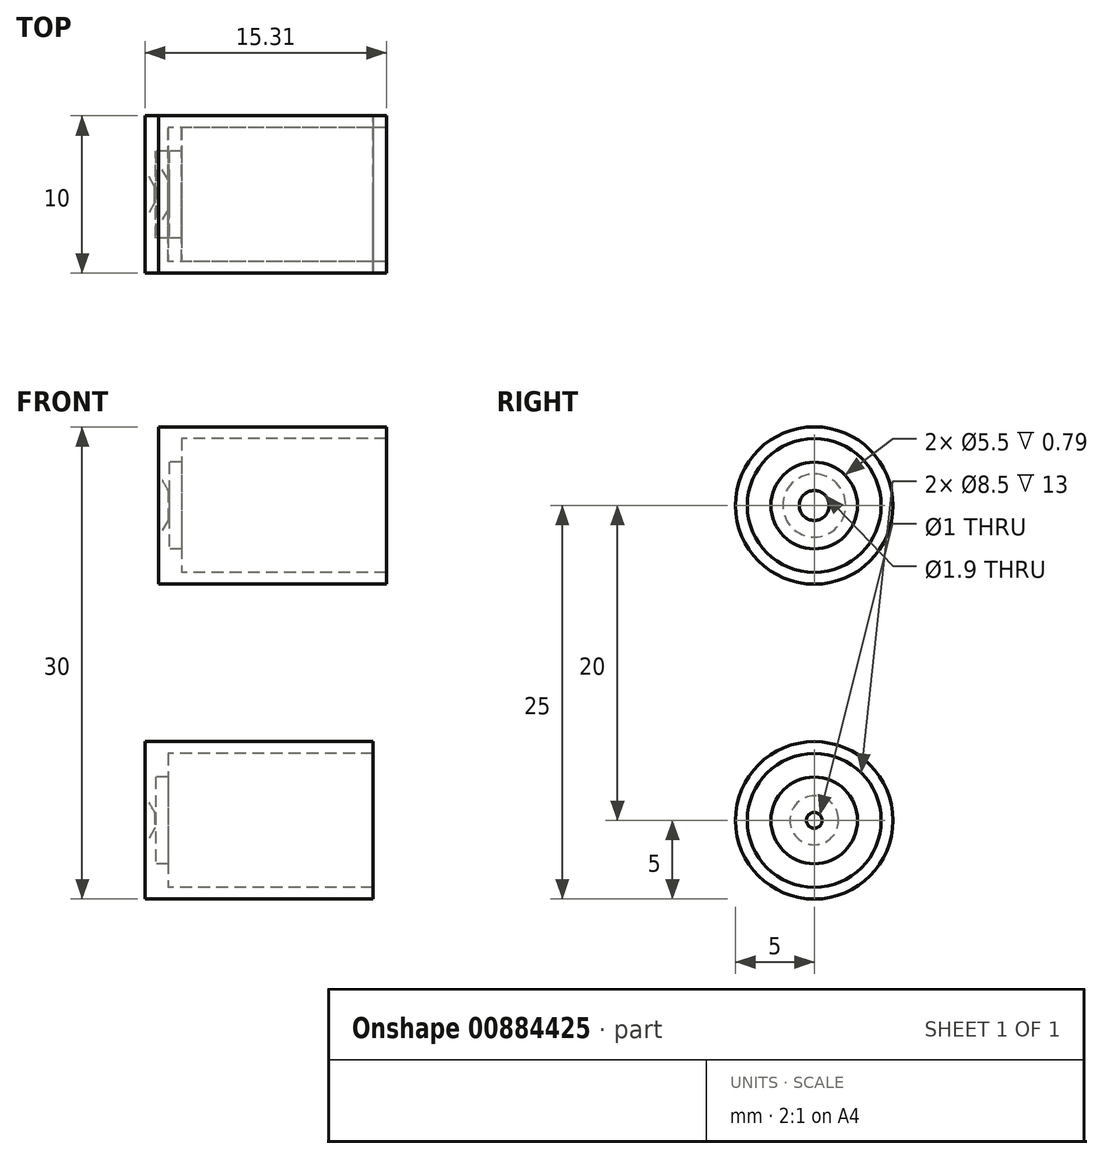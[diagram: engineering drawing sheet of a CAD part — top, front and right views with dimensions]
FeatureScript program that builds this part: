
annotation { "Feature Type Name" : "Feature", "Feature Type Description" : "" }
export const myFeature = defineFeature(function(context is Context, id is Id, definition is map)
    precondition{}
    {
        {
            var Q0;
            Q0=qCreatedBy(makeId("Front.planeOp"),FACE);
            var sketch = newSketch(context, id + "F0", { "sketchPlane" : qUnion([Q0])});
            skLineSegment(sketch, "E0", {"start": v(0, 0.95) * mm, "end": v(-0.6, 2) * mm});
            skLineSegment(sketch, "E1", {"start": v(-0.6, 2) * mm, "end": v(-0.6, 5) * mm});
            skLineSegment(sketch, "E2", {"start": v(-0.6, 5) * mm, "end": v(13.85, 5) * mm});
            skLineSegment(sketch, "E3", {"start": v(13.85, 5) * mm, "end": v(13.85, 4.25) * mm});
            skLineSegment(sketch, "E4", {"start": v(13.85, 4.25) * mm, "end": v(0.85, 4.25) * mm});
            skLineSegment(sketch, "E5", {"start": v(0.85, 4.25) * mm, "end": v(0.85, 2.75) * mm});
            skLineSegment(sketch, "E6", {"start": v(0.85, 2.75) * mm, "end": v(0.06, 2.75) * mm});
            skLineSegment(sketch, "E7", {"start": v(0.06, 2.75) * mm, "end": v(0.06, 0.95) * mm});
            skLineSegment(sketch, "E8", {"start": v(0.06, 0.95) * mm, "end": v(0, 0.95) * mm});
            skLineSegment(sketch, "E9", {"start": v(-4.1, 0) * mm, "end": v(8.34, 0) * mm, "construction": true});
            skLineSegment(sketch, "E10", {"start": v(-0.85, -19.5) * mm, "end": v(-1.46, -18.45) * mm});
            skLineSegment(sketch, "E11", {"start": v(-1.46, -18.45) * mm, "end": v(-1.46, -15) * mm});
            skLineSegment(sketch, "E12", {"start": v(-1.46, -15) * mm, "end": v(13, -15) * mm});
            skLineSegment(sketch, "E13", {"start": v(13, -15) * mm, "end": v(13, -15.75) * mm});
            skLineSegment(sketch, "E14", {"start": v(13, -15.75) * mm, "end": v(0, -15.75) * mm});
            skLineSegment(sketch, "E15", {"start": v(0, -15.75) * mm, "end": v(0, -17.25) * mm});
            skLineSegment(sketch, "E16", {"start": v(0, -17.25) * mm, "end": v(-0.79, -17.25) * mm});
            skLineSegment(sketch, "E17", {"start": v(-0.79, -17.25) * mm, "end": v(-0.79, -19.5) * mm});
            skLineSegment(sketch, "E18", {"start": v(-0.79, -19.5) * mm, "end": v(-0.85, -19.5) * mm});
            skLineSegment(sketch, "E19", {"start": v(-5.07, -20) * mm, "end": v(7.38, -20) * mm, "construction": true});
            skSolve(sketch);
        }
        {
            var Q0;
            Q0=makeQuery(id+"F0.imprint","IMPRINT",FACE,{"disambiguationData":[TD([[makeQuery(id+"F0.imprint","IMPRINT",EDGE,{"derivedFrom":sQuery(id+"F0.wireOp",EDGE,"E0")}),-1.0]])]});
            var Q1;
            Q1=sQuery(id+"F0.wireOp",EDGE,"E9");
            revolve(context, id + "F1", {"surfaceOperationType" : NewSurfaceOperationType.NEW, "entities" : qUnion([Q0]), "axis" : qUnion([Q1]), "revolveType" : RevolveType.FULL});
        }
        {
            var Q0;
            Q0=makeQuery(id+"F0.imprint","IMPRINT",FACE,{"disambiguationData":[TD([[makeQuery(id+"F0.imprint","IMPRINT",EDGE,{"derivedFrom":sQuery(id+"F0.wireOp",EDGE,"E10")}),-1.0]])]});
            var Q1;
            Q1=sQuery(id+"F0.wireOp",EDGE,"E19");
            revolve(context, id + "F2", {"surfaceOperationType" : NewSurfaceOperationType.NEW, "entities" : qUnion([Q0]), "axis" : qUnion([Q1]), "revolveType" : RevolveType.FULL});
        }
    });
